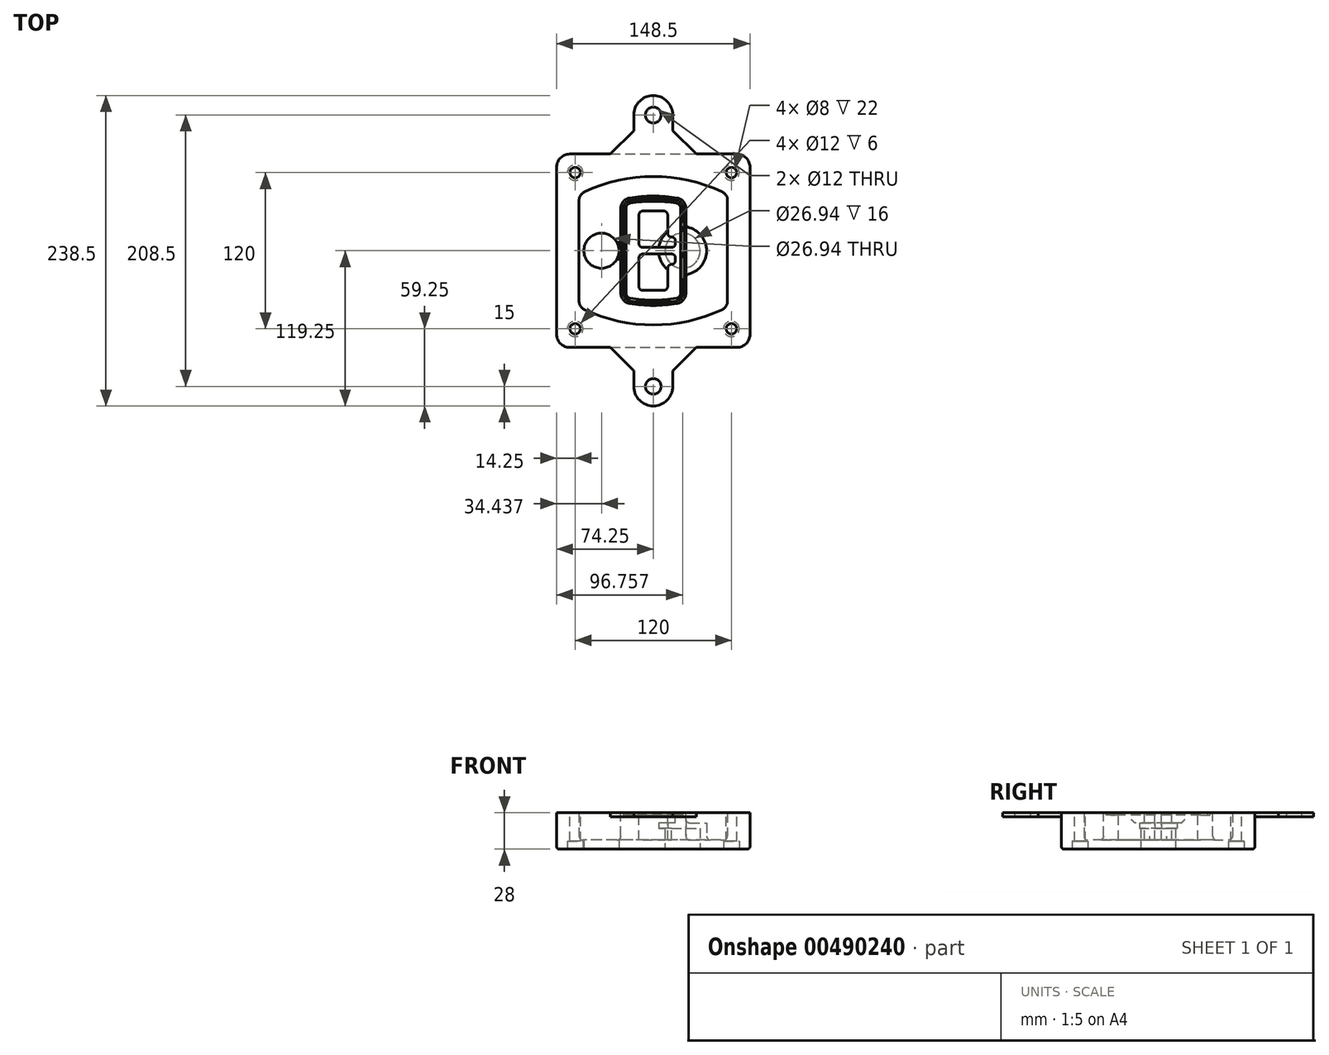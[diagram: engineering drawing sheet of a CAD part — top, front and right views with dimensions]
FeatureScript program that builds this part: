
annotation { "Feature Type Name" : "Feature", "Feature Type Description" : "" }
export const myFeature = defineFeature(function(context is Context, id is Id, definition is map)
    precondition{}
    {
        {
            var Q0;
            Q0=qCreatedBy(makeId("Top.planeOp"),FACE);
            var sketch = newSketch(context, id + "F0", { "sketchPlane" : qUnion([Q0])});
            skPoint(sketch, "E0.rect.middle", {"position": v(0, 0) * mm});
            skLineSegment(sketch, "E1.bottom", {"start": v(-64.25, -74.25) * mm, "end": v(64.25, -74.25) * mm});
            skLineSegment(sketch, "E1.top", {"start": v(-64.25, 74.25) * mm, "end": v(64.25, 74.25) * mm});
            skLineSegment(sketch, "E1.left", {"start": v(-74.25, -64.25) * mm, "end": v(-74.25, 64.25) * mm});
            skLineSegment(sketch, "E1.right", {"start": v(74.25, -64.25) * mm, "end": v(74.25, 64.25) * mm});
            skLineSegment(sketch, "E2", {"start": v(-74.25, 74.25) * mm, "end": v(74.25, -74.25) * mm, "construction": true});
            skLineSegment(sketch, "E3", {"start": v(74.25, 74.25) * mm, "end": v(-74.25, -74.25) * mm, "construction": true});
            skCircle(sketch, "E4", {"center": v(-60, 60) * mm, "radius": 4 * mm});
            skCircle(sketch, "E5", {"center": v(60, 60) * mm, "radius": 4 * mm});
            skCircle(sketch, "E6", {"center": v(60, -60) * mm, "radius": 4 * mm});
            skCircle(sketch, "E7", {"center": v(-60, -60) * mm, "radius": 4 * mm});
            skLineSegment(sketch, "E8", {"start": v(-60, 60) * mm, "end": v(60, 60) * mm, "construction": true});
            skLineSegment(sketch, "E9", {"start": v(60, 60) * mm, "end": v(60, -60) * mm, "construction": true});
            skLineSegment(sketch, "E10", {"start": v(60, -60) * mm, "end": v(-60, -60) * mm, "construction": true});
            skLineSegment(sketch, "E11", {"start": v(-60, -60) * mm, "end": v(-60, 60) * mm, "construction": true});
            skLineSegment(sketch, "E12", {"start": v(-60, 38.83) * mm, "end": v(-60, -38.83) * mm});
            skLineSegment(sketch, "E13", {"start": v(60, 38.83) * mm, "end": v(60, -38.83) * mm});
            skArc(sketch, "E14", {"start": v(54.26, 47.88) * mm, "mid": v(0, 60) * mm, "end": v(-54.26, 47.88) * mm});
            skArc(sketch, "E15", {"start": v(-54.26, -47.88) * mm, "mid": v(0, -60) * mm, "end": v(54.26, -47.88) * mm});
            skLineSegment(sketch, "E16", {"start": v(-60, 0) * mm, "end": v(60, 0) * mm, "construction": true});
            skPoint(sketch, "E17.visualSharp", {"position": v(-60, -45) * mm});
            skArc(sketch, "E17.filletArc", {"start": v(-60, -38.83) * mm, "mid": v(-58.44, -44.2) * mm, "end": v(-54.26, -47.88) * mm});
            skPoint(sketch, "E18.visualSharp", {"position": v(-60, 45) * mm});
            skArc(sketch, "E18.filletArc", {"start": v(-54.26, 47.88) * mm, "mid": v(-58.44, 44.2) * mm, "end": v(-60, 38.83) * mm});
            skPoint(sketch, "E19.visualSharp", {"position": v(60, 45) * mm});
            skArc(sketch, "E19.filletArc", {"start": v(60, 38.83) * mm, "mid": v(58.44, 44.2) * mm, "end": v(54.26, 47.88) * mm});
            skPoint(sketch, "E20.visualSharp", {"position": v(60, -45) * mm});
            skArc(sketch, "E20.filletArc", {"start": v(54.26, -47.88) * mm, "mid": v(58.44, -44.2) * mm, "end": v(60, -38.83) * mm});
            skPoint(sketch, "E21.visualSharp", {"position": v(-74.25, 74.25) * mm});
            skArc(sketch, "E21.filletArc", {"start": v(-64.25, 74.25) * mm, "mid": v(-71.32, 71.32) * mm, "end": v(-74.25, 64.25) * mm});
            skPoint(sketch, "E22.visualSharp", {"position": v(74.25, 74.25) * mm});
            skArc(sketch, "E22.filletArc", {"start": v(74.25, 64.25) * mm, "mid": v(71.32, 71.32) * mm, "end": v(64.25, 74.25) * mm});
            skPoint(sketch, "E23.visualSharp", {"position": v(74.25, -74.25) * mm});
            skArc(sketch, "E23.filletArc", {"start": v(64.25, -74.25) * mm, "mid": v(71.32, -71.32) * mm, "end": v(74.25, -64.25) * mm});
            skPoint(sketch, "E24.visualSharp", {"position": v(-74.25, -74.25) * mm});
            skArc(sketch, "E24.filletArc", {"start": v(-74.25, -64.25) * mm, "mid": v(-71.32, -71.32) * mm, "end": v(-64.25, -74.25) * mm});
            skArc(sketch, "E25.0", {"start": v(57, 38.83) * mm, "mid": v(55.9, 42.58) * mm, "end": v(52.98, 45.17) * mm});
            skLineSegment(sketch, "E25.1", {"start": v(57, 38.83) * mm, "end": v(57, -38.83) * mm});
            skArc(sketch, "E25.2", {"start": v(52.98, -45.17) * mm, "mid": v(55.9, -42.58) * mm, "end": v(57, -38.83) * mm});
            skArc(sketch, "E25.3", {"start": v(-52.98, -45.17) * mm, "mid": v(0, -57) * mm, "end": v(52.98, -45.17) * mm});
            skArc(sketch, "E25.4", {"start": v(-57, -38.83) * mm, "mid": v(-55.9, -42.58) * mm, "end": v(-52.98, -45.17) * mm});
            skArc(sketch, "E25.5", {"start": v(52.98, 45.17) * mm, "mid": v(0, 57) * mm, "end": v(-52.98, 45.17) * mm});
            skLineSegment(sketch, "E25.6", {"start": v(-57, 38.83) * mm, "end": v(-57, -38.83) * mm});
            skArc(sketch, "E25.7", {"start": v(-52.98, 45.17) * mm, "mid": v(-55.9, 42.58) * mm, "end": v(-57, 38.83) * mm});
            skArc(sketch, "E26.0", {"start": v(-55.96, 51.5) * mm, "mid": v(-61.82, 46.33) * mm, "end": v(-64, 38.83) * mm});
            skArc(sketch, "E26.1", {"start": v(55.96, 51.5) * mm, "mid": v(0, 64) * mm, "end": v(-55.96, 51.5) * mm});
            skArc(sketch, "E26.2", {"start": v(64, 38.83) * mm, "mid": v(61.82, 46.33) * mm, "end": v(55.96, 51.5) * mm});
            skLineSegment(sketch, "E26.3", {"start": v(64, 38.83) * mm, "end": v(64, -38.83) * mm});
            skArc(sketch, "E26.4", {"start": v(55.96, -51.5) * mm, "mid": v(61.82, -46.33) * mm, "end": v(64, -38.83) * mm});
            skLineSegment(sketch, "E26.5", {"start": v(-64, 38.83) * mm, "end": v(-64, -38.83) * mm});
            skArc(sketch, "E26.6", {"start": v(-55.96, -51.5) * mm, "mid": v(0, -64) * mm, "end": v(55.96, -51.5) * mm});
            skArc(sketch, "E26.7", {"start": v(-64, -38.83) * mm, "mid": v(-61.82, -46.33) * mm, "end": v(-55.96, -51.5) * mm});
            skSolve(sketch);
        }
        {
            var Q0;
            Q0=makeQuery(id+"F0.imprint","IMPRINT",FACE,{"disambiguationData":[TD([[makeQuery(id+"F0.imprint","IMPRINT",EDGE,{"derivedFrom":sQuery(id+"F0.wireOp",EDGE,"E1.bottom")}),1.0]])]});
            var Q1;
            Q1=makeQuery(id+"F0.imprint","IMPRINT",FACE,{"disambiguationData":[TD([[makeQuery(id+"F0.imprint","IMPRINT",EDGE,{"derivedFrom":sQuery(id+"F0.wireOp",EDGE,"E12")}),1.0]])]});
            var Q2;
            Q2=makeQuery(id+"F0.imprint","IMPRINT",FACE,{"disambiguationData":[TD([[makeQuery(id+"F0.imprint","IMPRINT",EDGE,{"derivedFrom":sQuery(id+"F0.wireOp",EDGE,"E25.0")}),1.0]])]});
            var Q3;
            Q3=makeQuery(id+"F0.imprint","IMPRINT",FACE,{"disambiguationData":[TD([[makeQuery(id+"F0.imprint","IMPRINT",EDGE,{"derivedFrom":sQuery(id+"F0.wireOp",EDGE,"E12")}),-1.0]])]});
            extrude(context, id + "F1", {"entities" : qUnion([Q0, Q1, Q2, Q3]), "oppositeDirection" : true, "depth" : 25 * mm});
        }
        {
            var Q0;
            Q0=makeQuery(id+"F0.imprint","IMPRINT",FACE,{"disambiguationData":[TD([[makeQuery(id+"F0.imprint","IMPRINT",EDGE,{"derivedFrom":sQuery(id+"F0.wireOp",EDGE,"E12")}),1.0]])]});
            extrude(context, id + "F2", {"entities" : qUnion([Q0]), "operationType" : NewBodyOperationType.ADD, "depth" : 3 * mm});
        }
        {
            var Q0;
            Q0=makeQuery(id+"F0.imprint","IMPRINT",FACE,{"disambiguationData":[TD([[makeQuery(id+"F0.imprint","IMPRINT",EDGE,{"derivedFrom":sQuery(id+"F0.wireOp",EDGE,"E25.0")}),1.0]])]});
            extrude(context, id + "F3", {"entities" : qUnion([Q0]), "operationType" : NewBodyOperationType.REMOVE, "oppositeDirection" : true, "depth" : 18 * mm});
        }
        {
            var Q0;
            Q0=makeQuery(id+"F2.opExtrude","CAP_FACE",FACE,{"disambiguationData":[OSD([sQuery(id+"F0.wireOp",EDGE,"E12"),sQuery(id+"F0.wireOp",EDGE,"E13"),sQuery(id+"F0.wireOp",EDGE,"E14"),sQuery(id+"F0.wireOp",EDGE,"E15"),sQuery(id+"F0.wireOp",EDGE,"E17.filletArc"),sQuery(id+"F0.wireOp",EDGE,"E18.filletArc"),sQuery(id+"F0.wireOp",EDGE,"E19.filletArc"),sQuery(id+"F0.wireOp",EDGE,"E20.filletArc"),sQuery(id+"F0.wireOp",EDGE,"E25.0"),sQuery(id+"F0.wireOp",EDGE,"E25.1"),sQuery(id+"F0.wireOp",EDGE,"E25.2"),sQuery(id+"F0.wireOp",EDGE,"E25.3"),sQuery(id+"F0.wireOp",EDGE,"E25.4"),sQuery(id+"F0.wireOp",EDGE,"E25.5"),sQuery(id+"F0.wireOp",EDGE,"E25.6"),sQuery(id+"F0.wireOp",EDGE,"E25.7")])],"isStart":false});
            var sketch = newSketch(context, id + "F4", { "sketchPlane" : qUnion([Q0])});
            skArc(sketch, "E27.0", {"start": v(-18.34, -40.45) * mm, "mid": v(0, -42) * mm, "end": v(18.34, -40.45) * mm});
            skArc(sketch, "E28.0", {"start": v(18.34, 40.45) * mm, "mid": v(0, 42) * mm, "end": v(-18.34, 40.45) * mm});
            skLineSegment(sketch, "E29", {"start": v(-25, 32.57) * mm, "end": v(-25, -32.57) * mm});
            skLineSegment(sketch, "E30", {"start": v(25, 32.57) * mm, "end": v(25, -32.57) * mm});
            skLineSegment(sketch, "E31", {"start": v(-25, 39.1) * mm, "end": v(25, 39.1) * mm, "construction": true});
            skLineSegment(sketch, "E32", {"start": v(-25, -39.1) * mm, "end": v(25, -39.1) * mm, "construction": true});
            skPoint(sketch, "E33.visualSharp", {"position": v(-25, 39.1) * mm});
            skArc(sketch, "E33.filletArc", {"start": v(-18.34, 40.45) * mm, "mid": v(-23.11, 37.73) * mm, "end": v(-25, 32.57) * mm});
            skPoint(sketch, "E34.visualSharp", {"position": v(25, 39.1) * mm});
            skArc(sketch, "E34.filletArc", {"start": v(25, 32.57) * mm, "mid": v(23.11, 37.73) * mm, "end": v(18.34, 40.45) * mm});
            skPoint(sketch, "E35.visualSharp", {"position": v(25, -39.1) * mm});
            skArc(sketch, "E35.filletArc", {"start": v(18.34, -40.45) * mm, "mid": v(23.11, -37.73) * mm, "end": v(25, -32.57) * mm});
            skPoint(sketch, "E36.visualSharp", {"position": v(-25, -39.1) * mm});
            skArc(sketch, "E36.filletArc", {"start": v(-25, -32.57) * mm, "mid": v(-23.11, -37.73) * mm, "end": v(-18.34, -40.45) * mm});
            skArc(sketch, "E37.0", {"start": v(52.98, 45.17) * mm, "mid": v(0, 57) * mm, "end": v(-52.98, 45.17) * mm});
            skArc(sketch, "E37.1", {"start": v(-52.98, 45.17) * mm, "mid": v(-55.9, 42.58) * mm, "end": v(-57, 38.83) * mm});
            skLineSegment(sketch, "E37.2", {"start": v(-57, 38.83) * mm, "end": v(-57, -38.83) * mm});
            skArc(sketch, "E37.3", {"start": v(-57, -38.83) * mm, "mid": v(-55.9, -42.58) * mm, "end": v(-52.98, -45.17) * mm});
            skArc(sketch, "E37.4", {"start": v(-52.98, -45.17) * mm, "mid": v(0, -57) * mm, "end": v(52.98, -45.17) * mm});
            skArc(sketch, "E37.5", {"start": v(52.98, -45.17) * mm, "mid": v(55.9, -42.58) * mm, "end": v(57, -38.83) * mm});
            skLineSegment(sketch, "E37.6", {"start": v(57, 38.83) * mm, "end": v(57, -38.83) * mm});
            skArc(sketch, "E37.7", {"start": v(57, 38.83) * mm, "mid": v(55.9, 42.58) * mm, "end": v(52.98, 45.17) * mm});
            skLineSegment(sketch, "E38.0", {"start": v(23, 32.57) * mm, "end": v(23, -32.57) * mm});
            skArc(sketch, "E38.1", {"start": v(18, -38.48) * mm, "mid": v(21.58, -36.44) * mm, "end": v(23, -32.57) * mm});
            skArc(sketch, "E38.2", {"start": v(-18, -38.48) * mm, "mid": v(0, -40) * mm, "end": v(18, -38.48) * mm});
            skArc(sketch, "E38.3", {"start": v(-23, -32.57) * mm, "mid": v(-21.58, -36.44) * mm, "end": v(-18, -38.48) * mm});
            skLineSegment(sketch, "E38.4", {"start": v(-23, 32.57) * mm, "end": v(-23, -32.57) * mm});
            skArc(sketch, "E38.5", {"start": v(23, 32.57) * mm, "mid": v(21.58, 36.44) * mm, "end": v(18, 38.48) * mm});
            skArc(sketch, "E38.6", {"start": v(-18, 38.48) * mm, "mid": v(-21.58, 36.44) * mm, "end": v(-23, 32.57) * mm});
            skArc(sketch, "E38.7", {"start": v(18, 38.48) * mm, "mid": v(0, 40) * mm, "end": v(-18, 38.48) * mm});
            skArc(sketch, "E39.0", {"start": v(21, 32.57) * mm, "mid": v(20.06, 35.15) * mm, "end": v(17.67, 36.5) * mm});
            skLineSegment(sketch, "E39.1", {"start": v(21, 32.57) * mm, "end": v(21, -32.57) * mm});
            skArc(sketch, "E39.2", {"start": v(17.67, -36.5) * mm, "mid": v(20.06, -35.15) * mm, "end": v(21, -32.57) * mm});
            skArc(sketch, "E39.3", {"start": v(-17.67, -36.5) * mm, "mid": v(0, -38) * mm, "end": v(17.67, -36.5) * mm});
            skArc(sketch, "E39.4", {"start": v(-21, -32.57) * mm, "mid": v(-20.06, -35.15) * mm, "end": v(-17.67, -36.5) * mm});
            skArc(sketch, "E39.5", {"start": v(17.67, 36.5) * mm, "mid": v(0, 38) * mm, "end": v(-17.67, 36.5) * mm});
            skLineSegment(sketch, "E39.6", {"start": v(-21, 32.57) * mm, "end": v(-21, -32.57) * mm});
            skArc(sketch, "E39.7", {"start": v(-17.67, 36.5) * mm, "mid": v(-20.06, 35.15) * mm, "end": v(-21, 32.57) * mm});
            skLineSegment(sketch, "E40", {"start": v(-25, 0) * mm, "end": v(25, 0) * mm, "construction": true});
            skLineSegment(sketch, "E41", {"start": v(-11, 5.5) * mm, "end": v(-11, 27.5) * mm});
            skLineSegment(sketch, "E42", {"start": v(-8, 30.5) * mm, "end": v(8, 30.5) * mm});
            skLineSegment(sketch, "E43", {"start": v(11, 27.5) * mm, "end": v(11, 13.5) * mm});
            skLineSegment(sketch, "E44", {"start": v(14, 10.5) * mm, "end": v(14, 10.5) * mm});
            skLineSegment(sketch, "E45", {"start": v(17, 7.5) * mm, "end": v(17, 5.5) * mm});
            skLineSegment(sketch, "E46", {"start": v(14, 2.5) * mm, "end": v(-8, 2.5) * mm});
            skPoint(sketch, "E47.visualSharp", {"position": v(-11, 30.5) * mm});
            skArc(sketch, "E47.filletArc", {"start": v(-8, 30.5) * mm, "mid": v(-10.12, 29.62) * mm, "end": v(-11, 27.5) * mm});
            skPoint(sketch, "E48.visualSharp", {"position": v(11, 30.5) * mm});
            skArc(sketch, "E48.filletArc", {"start": v(11, 27.5) * mm, "mid": v(10.12, 29.62) * mm, "end": v(8, 30.5) * mm});
            skPoint(sketch, "E49.visualSharp", {"position": v(11, 10.5) * mm});
            skArc(sketch, "E49.filletArc", {"start": v(11, 13.5) * mm, "mid": v(11.88, 11.38) * mm, "end": v(14, 10.5) * mm});
            skPoint(sketch, "E50.visualSharp", {"position": v(17, 10.5) * mm});
            skArc(sketch, "E50.filletArc", {"start": v(17, 7.5) * mm, "mid": v(16.12, 9.62) * mm, "end": v(14, 10.5) * mm});
            skPoint(sketch, "E51.visualSharp", {"position": v(17, 2.5) * mm});
            skArc(sketch, "E51.filletArc", {"start": v(14, 2.5) * mm, "mid": v(16.12, 3.38) * mm, "end": v(17, 5.5) * mm});
            skPoint(sketch, "E52.visualSharp", {"position": v(-11, 2.5) * mm});
            skArc(sketch, "E52.filletArc", {"start": v(-11, 5.5) * mm, "mid": v(-10.12, 3.38) * mm, "end": v(-8, 2.5) * mm});
            skLineSegment(sketch, "E53.0.MirrorCS", {"start": v(14, -2.5) * mm, "end": v(-8, -2.5) * mm});
            skArc(sketch, "E54.0.MirrorCS", {"start": v(-11, -5.5) * mm, "mid": v(-10.12, -3.38) * mm, "end": v(-8, -2.5) * mm});
            skLineSegment(sketch, "E55.0.MirrorCS", {"start": v(-11, -5.5) * mm, "end": v(-11, -27.5) * mm});
            skArc(sketch, "E56.0.MirrorCS", {"start": v(-8, -30.5) * mm, "mid": v(-10.12, -29.62) * mm, "end": v(-11, -27.5) * mm});
            skLineSegment(sketch, "E57.0.MirrorCS", {"start": v(-8, -30.5) * mm, "end": v(8, -30.5) * mm});
            skArc(sketch, "E58.0.MirrorCS", {"start": v(11, -27.5) * mm, "mid": v(10.12, -29.62) * mm, "end": v(8, -30.5) * mm});
            skLineSegment(sketch, "E59.0.MirrorCS", {"start": v(11, -27.5) * mm, "end": v(11, -13.5) * mm});
            skArc(sketch, "E60.0.MirrorCS", {"start": v(11, -13.5) * mm, "mid": v(11.88, -11.38) * mm, "end": v(14, -10.5) * mm});
            skArc(sketch, "E61.0.MirrorCS", {"start": v(17, -7.5) * mm, "mid": v(16.12, -9.62) * mm, "end": v(14, -10.5) * mm});
            skLineSegment(sketch, "E62.0.MirrorCS", {"start": v(17, -7.5) * mm, "end": v(17, -5.5) * mm});
            skArc(sketch, "E63.0.MirrorCS", {"start": v(14, -2.5) * mm, "mid": v(16.12, -3.38) * mm, "end": v(17, -5.5) * mm});
            skSolve(sketch);
        }
        {
            var Q0;
            Q0=makeQuery(id+"F4.imprint","IMPRINT",FACE,{"disambiguationData":[TD([[makeQuery(id+"F4.imprint","IMPRINT",EDGE,{"derivedFrom":sQuery(id+"F4.wireOp",EDGE,"E27.0")}),1.0]])]});
            var Q1;
            Q1=makeQuery(id+"F4.imprint","IMPRINT",FACE,{"disambiguationData":[TD([[makeQuery(id+"F4.imprint","IMPRINT",EDGE,{"derivedFrom":sQuery(id+"F4.wireOp",EDGE,"E38.0")}),-1.0]])]});
            var Q2;
            Q2=makeQuery(id+"F4.imprint","IMPRINT",FACE,{"disambiguationData":[TD([[makeQuery(id+"F4.imprint","IMPRINT",EDGE,{"derivedFrom":sQuery(id+"F4.wireOp",EDGE,"E39.0")}),1.0]])]});
            extrude(context, id + "F5", {"entities" : qUnion([Q0, Q1, Q2]), "operationType" : NewBodyOperationType.ADD, "endBound" : BoundingType.UP_TO_NEXT, "oppositeDirection" : true, "depth" : 25 * mm});
        }
        {
            var Q0;
            Q0=makeQuery(id+"F4.imprint","IMPRINT",FACE,{"disambiguationData":[TD([[makeQuery(id+"F4.imprint","IMPRINT",EDGE,{"derivedFrom":sQuery(id+"F4.wireOp",EDGE,"E38.0")}),-1.0]])]});
            extrude(context, id + "F6", {"entities" : qUnion([Q0]), "operationType" : NewBodyOperationType.REMOVE, "oppositeDirection" : true, "depth" : 2 * mm});
        }
        {
            var Q0;
            Q0=makeQuery(id+"F1.opExtrude","CAP_FACE",FACE,{"disambiguationData":[OSD([sQuery(id+"F0.wireOp",EDGE,"E1.bottom"),sQuery(id+"F0.wireOp",EDGE,"E1.top"),sQuery(id+"F0.wireOp",EDGE,"E1.left"),sQuery(id+"F0.wireOp",EDGE,"E1.right"),sQuery(id+"F0.wireOp",EDGE,"E4"),sQuery(id+"F0.wireOp",EDGE,"E5"),sQuery(id+"F0.wireOp",EDGE,"E6"),sQuery(id+"F0.wireOp",EDGE,"E7"),sQuery(id+"F0.wireOp",EDGE,"E21.filletArc"),sQuery(id+"F0.wireOp",EDGE,"E22.filletArc"),sQuery(id+"F0.wireOp",EDGE,"E23.filletArc"),sQuery(id+"F0.wireOp",EDGE,"E24.filletArc")])],"isStart":false});
            var sketch = newSketch(context, id + "F7", { "sketchPlane" : qUnion([Q0])});
            skCircle(sketch, "E64", {"center": v(22.5, 0) * mm, "radius": 13.47 * mm});
            skCircle(sketch, "E65", {"center": v(-39.81, 0) * mm, "radius": 13.47 * mm});
            skLineSegment(sketch, "E66", {"start": v(74.25, 0) * mm, "end": v(-74.25, 0) * mm});
            skCircle(sketch, "E67", {"center": v(22.5, 0) * mm, "radius": 18.47 * mm});
            skCircle(sketch, "E68", {"center": v(60, -60) * mm, "radius": 6 * mm});
            skCircle(sketch, "E69", {"center": v(-60, -60) * mm, "radius": 6 * mm});
            skCircle(sketch, "E70", {"center": v(-60, 60) * mm, "radius": 6 * mm});
            skCircle(sketch, "E71", {"center": v(60, 60) * mm, "radius": 6 * mm});
            skSolve(sketch);
        }
        {
            var Q0;
            {var subQ1=sQuery(id+"F7.wireOp",EDGE,"E66");var subQ4=sQuery(id+"F7.wireOp",EDGE,"E64");var subQ6=makeQuery(id+"F7.imprint","INTERSECT",VERTEX,{"disambiguationData":[OD(0.0)],"derivedFrom":[subQ4,subQ1]});Q0=makeQuery(id+"F7.imprint","IMPRINT",FACE,{"disambiguationData":[TD([[makeQuery(id+"F7.imprint","IMPRINT",EDGE,{"disambiguationData":[TD([[subQ6,-1.0]])],"derivedFrom":subQ4}),-1.0]])]});}
            var Q1;
            {var subQ0=sQuery(id+"F7.wireOp",EDGE,"E66");var subQ1=sQuery(id+"F7.wireOp",EDGE,"E64");var subQ3=makeQuery(id+"F7.imprint","INTERSECT",VERTEX,{"disambiguationData":[OD(0.0)],"derivedFrom":[subQ1,subQ0]});Q1=makeQuery(id+"F7.imprint","IMPRINT",FACE,{"disambiguationData":[TD([[makeQuery(id+"F7.imprint","IMPRINT",EDGE,{"disambiguationData":[TD([[subQ3,-1.0]])],"derivedFrom":subQ1}),1.0]])]});}
            var Q2;
            {var subQ0=sQuery(id+"F7.wireOp",EDGE,"E66");var subQ1=sQuery(id+"F7.wireOp",EDGE,"E64");var subQ3=makeQuery(id+"F7.imprint","INTERSECT",VERTEX,{"disambiguationData":[OD(0.0)],"derivedFrom":[subQ1,subQ0]});Q2=makeQuery(id+"F7.imprint","IMPRINT",FACE,{"disambiguationData":[TD([[makeQuery(id+"F7.imprint","IMPRINT",EDGE,{"disambiguationData":[TD([[subQ3,1.0]])],"derivedFrom":subQ1}),1.0]])]});}
            var Q3;
            {var subQ1=sQuery(id+"F7.wireOp",EDGE,"E66");var subQ4=sQuery(id+"F7.wireOp",EDGE,"E64");var subQ6=makeQuery(id+"F7.imprint","INTERSECT",VERTEX,{"disambiguationData":[OD(0.0)],"derivedFrom":[subQ4,subQ1]});Q3=makeQuery(id+"F7.imprint","IMPRINT",FACE,{"disambiguationData":[TD([[makeQuery(id+"F7.imprint","IMPRINT",EDGE,{"disambiguationData":[TD([[subQ6,1.0]])],"derivedFrom":subQ4}),-1.0]])]});}
            extrude(context, id + "F8", {"entities" : qUnion([Q0, Q1, Q2, Q3]), "operationType" : NewBodyOperationType.ADD, "oppositeDirection" : true, "depth" : 20 * mm});
        }
        {
            var Q0;
            {var subQ0=sQuery(id+"F7.wireOp",EDGE,"E66");var subQ1=sQuery(id+"F7.wireOp",EDGE,"E64");var subQ3=makeQuery(id+"F7.imprint","INTERSECT",VERTEX,{"disambiguationData":[OD(0.0)],"derivedFrom":[subQ1,subQ0]});Q0=makeQuery(id+"F7.imprint","IMPRINT",FACE,{"disambiguationData":[TD([[makeQuery(id+"F7.imprint","IMPRINT",EDGE,{"disambiguationData":[TD([[subQ3,-1.0]])],"derivedFrom":subQ1}),1.0]])]});}
            var Q1;
            {var subQ0=sQuery(id+"F7.wireOp",EDGE,"E66");var subQ1=sQuery(id+"F7.wireOp",EDGE,"E64");var subQ3=makeQuery(id+"F7.imprint","INTERSECT",VERTEX,{"disambiguationData":[OD(0.0)],"derivedFrom":[subQ1,subQ0]});Q1=makeQuery(id+"F7.imprint","IMPRINT",FACE,{"disambiguationData":[TD([[makeQuery(id+"F7.imprint","IMPRINT",EDGE,{"disambiguationData":[TD([[subQ3,1.0]])],"derivedFrom":subQ1}),1.0]])]});}
            extrude(context, id + "F9", {"entities" : qUnion([Q0, Q1]), "operationType" : NewBodyOperationType.REMOVE, "oppositeDirection" : true, "depth" : 16 * mm});
        }
        {
            var Q0;
            {var subQ0=sQuery(id+"F7.wireOp",EDGE,"E66");var subQ1=sQuery(id+"F7.wireOp",EDGE,"E65");var subQ3=makeQuery(id+"F7.imprint","INTERSECT",VERTEX,{"disambiguationData":[OD(0.0)],"derivedFrom":[subQ1,subQ0]});Q0=makeQuery(id+"F7.imprint","IMPRINT",FACE,{"disambiguationData":[TD([[makeQuery(id+"F7.imprint","IMPRINT",EDGE,{"disambiguationData":[TD([[subQ3,-1.0]])],"derivedFrom":subQ1}),1.0]])]});}
            var Q1;
            {var subQ0=sQuery(id+"F7.wireOp",EDGE,"E66");var subQ1=sQuery(id+"F7.wireOp",EDGE,"E65");var subQ3=makeQuery(id+"F7.imprint","INTERSECT",VERTEX,{"disambiguationData":[OD(0.0)],"derivedFrom":[subQ1,subQ0]});Q1=makeQuery(id+"F7.imprint","IMPRINT",FACE,{"disambiguationData":[TD([[makeQuery(id+"F7.imprint","IMPRINT",EDGE,{"disambiguationData":[TD([[subQ3,1.0]])],"derivedFrom":subQ1}),1.0]])]});}
            extrude(context, id + "F10", {"entities" : qUnion([Q0, Q1]), "operationType" : NewBodyOperationType.REMOVE, "oppositeDirection" : true, "depth" : 25 * mm});
        }
        {
            var Q0;
            Q0=makeQuery(id+"F7.imprint","IMPRINT",FACE,{"disambiguationData":[TD([[makeQuery(id+"F7.imprint","IMPRINT",EDGE,{"derivedFrom":sQuery(id+"F7.wireOp",EDGE,"E68")}),1.0]])]});
            var Q1;
            Q1=makeQuery(id+"F7.imprint","IMPRINT",FACE,{"disambiguationData":[TD([[makeQuery(id+"F7.imprint","IMPRINT",EDGE,{"derivedFrom":makeQuery(id+"F1.opExtrude","CAP_EDGE",EDGE,{"disambiguationData":[OSD([sQuery(id+"F0.wireOp",EDGE,"E5")])],"isStart":false})}),-1.0]])]});
            var Q2;
            Q2=makeQuery(id+"F7.imprint","IMPRINT",FACE,{"disambiguationData":[TD([[makeQuery(id+"F7.imprint","IMPRINT",EDGE,{"derivedFrom":sQuery(id+"F7.wireOp",EDGE,"E69")}),1.0]])]});
            var Q3;
            Q3=makeQuery(id+"F7.imprint","IMPRINT",FACE,{"disambiguationData":[TD([[makeQuery(id+"F7.imprint","IMPRINT",EDGE,{"derivedFrom":makeQuery(id+"F1.opExtrude","CAP_EDGE",EDGE,{"disambiguationData":[OSD([sQuery(id+"F0.wireOp",EDGE,"E4")])],"isStart":false})}),-1.0]])]});
            var Q4;
            Q4=makeQuery(id+"F7.imprint","IMPRINT",FACE,{"disambiguationData":[TD([[makeQuery(id+"F7.imprint","IMPRINT",EDGE,{"derivedFrom":sQuery(id+"F7.wireOp",EDGE,"E70")}),1.0]])]});
            var Q5;
            Q5=makeQuery(id+"F7.imprint","IMPRINT",FACE,{"disambiguationData":[TD([[makeQuery(id+"F7.imprint","IMPRINT",EDGE,{"derivedFrom":makeQuery(id+"F1.opExtrude","CAP_EDGE",EDGE,{"disambiguationData":[OSD([sQuery(id+"F0.wireOp",EDGE,"E7")])],"isStart":false})}),-1.0]])]});
            var Q6;
            Q6=makeQuery(id+"F7.imprint","IMPRINT",FACE,{"disambiguationData":[TD([[makeQuery(id+"F7.imprint","IMPRINT",EDGE,{"derivedFrom":sQuery(id+"F7.wireOp",EDGE,"E71")}),1.0]])]});
            var Q7;
            Q7=makeQuery(id+"F7.imprint","IMPRINT",FACE,{"disambiguationData":[TD([[makeQuery(id+"F7.imprint","IMPRINT",EDGE,{"derivedFrom":makeQuery(id+"F1.opExtrude","CAP_EDGE",EDGE,{"disambiguationData":[OSD([sQuery(id+"F0.wireOp",EDGE,"E6")])],"isStart":false})}),-1.0]])]});
            extrude(context, id + "F11", {"entities" : qUnion([Q0, Q1, Q2, Q3, Q4, Q5, Q6, Q7]), "operationType" : NewBodyOperationType.REMOVE, "oppositeDirection" : true, "depth" : 6 * mm});
        }
        {
            var Q0;
            Q0=makeQuery(id+"F9.boolean.opBoolean","COPY",FACE,{"derivedFrom":makeQuery(id+"F9.opExtrude","CAP_FACE",FACE,{"disambiguationData":[OSD([sQuery(id+"F7.wireOp",EDGE,"E64")])],"isStart":false})});
            var sketch = newSketch(context, id + "F12", { "sketchPlane" : qUnion([Q0])});
            skArc(sketch, "E72.0", {"start": v(11, 14.45) * mm, "mid": v(6.45, 9.13) * mm, "end": v(4.2, 2.5) * mm});
            skArc(sketch, "E72.1", {"start": v(4.2, -2.5) * mm, "mid": v(6.45, -9.13) * mm, "end": v(11, -14.45) * mm});
            skLineSegment(sketch, "E73", {"start": v(4.2, -2.5) * mm, "end": v(14, -2.5) * mm});
            skLineSegment(sketch, "E74.0", {"start": v(14, 2.5) * mm, "end": v(4.2, 2.5) * mm});
            skArc(sketch, "E74.1", {"start": v(14, 2.5) * mm, "mid": v(16.12, 3.38) * mm, "end": v(17, 5.5) * mm});
            skLineSegment(sketch, "E74.2", {"start": v(17, 7.5) * mm, "end": v(17, 5.5) * mm});
            skArc(sketch, "E74.3", {"start": v(17, 7.5) * mm, "mid": v(16.12, 9.62) * mm, "end": v(14, 10.5) * mm});
            skArc(sketch, "E74.4", {"start": v(11, 13.5) * mm, "mid": v(11.88, 11.38) * mm, "end": v(14, 10.5) * mm});
            skLineSegment(sketch, "E74.5", {"start": v(11, 14.45) * mm, "end": v(11, 13.5) * mm});
            skLineSegment(sketch, "E74.7", {"start": v(14, -2.5) * mm, "end": v(4.2, -2.5) * mm});
            skArc(sketch, "E74.8", {"start": v(14, -2.5) * mm, "mid": v(16.12, -3.38) * mm, "end": v(17, -5.5) * mm});
            skLineSegment(sketch, "E74.9", {"start": v(17, -7.5) * mm, "end": v(17, -5.5) * mm});
            skArc(sketch, "E74.10", {"start": v(17, -7.5) * mm, "mid": v(16.12, -9.62) * mm, "end": v(14, -10.5) * mm});
            skArc(sketch, "E74.11", {"start": v(11, -13.5) * mm, "mid": v(11.88, -11.38) * mm, "end": v(14, -10.5) * mm});
            skLineSegment(sketch, "E74.12", {"start": v(11, -14.45) * mm, "end": v(11, -13.5) * mm});
            skPoint(sketch, "E75.orphan", {"position": v(11, -27.5) * mm});
            skPoint(sketch, "E76.orphan", {"position": v(-8, -2.5) * mm});
            skPoint(sketch, "E77.orphan", {"position": v(-8, 2.5) * mm});
            skPoint(sketch, "E78.orphan", {"position": v(11, 27.5) * mm});
            skSolve(sketch);
        }
        {
            var Q0;
            {var subQ7=sQuery(id+"F12.wireOp",EDGE,"E72.0");var subQ14=sQuery(id+"F12.wireOp",EDGE,"E72.1");var subQ16=sQuery(id+"F12.wireOp",EDGE,"E74.1");var subQ18=sQuery(id+"F12.wireOp",EDGE,"E74.8");Q0=qUnion([makeQuery(id+"F12.imprint","IMPRINT",FACE,{"disambiguationData":[TD([[makeQuery(id+"F12.imprint","IMPRINT",EDGE,{"derivedFrom":subQ7}),1.0]])]}),makeQuery(id+"F12.imprint","IMPRINT",FACE,{"disambiguationData":[TD([[makeQuery(id+"F12.imprint","IMPRINT",EDGE,{"derivedFrom":subQ14}),1.0]])]}),makeQuery(id+"F12.imprint","IMPRINT",FACE,{"disambiguationData":[TD([[makeQuery(id+"F12.imprint","IMPRINT",EDGE,{"derivedFrom":subQ16}),1.0]])]}),makeQuery(id+"F12.imprint","IMPRINT",FACE,{"disambiguationData":[TD([[makeQuery(id+"F12.imprint","IMPRINT",EDGE,{"derivedFrom":subQ18}),-1.0]])]})]);}
            var Q1;
            Q1=makeQuery(id+"F5.boolean.opBoolean","SPLIT",FACE,{"disambiguationData":[TD([makeQuery(id+"F5.opExtrude","SWEPT_FACE",FACE,{"disambiguationData":[OSD([sQuery(id+"F4.wireOp",EDGE,"E41")])]})])],"derivedFrom":makeQuery(id+"F3.boolean.opBoolean","COPY",FACE,{"derivedFrom":makeQuery(id+"F3.opExtrude","CAP_FACE",FACE,{"disambiguationData":[OSD([sQuery(id+"F0.wireOp",EDGE,"E25.0"),sQuery(id+"F0.wireOp",EDGE,"E25.1"),sQuery(id+"F0.wireOp",EDGE,"E25.2"),sQuery(id+"F0.wireOp",EDGE,"E25.3"),sQuery(id+"F0.wireOp",EDGE,"E25.4"),sQuery(id+"F0.wireOp",EDGE,"E25.5"),sQuery(id+"F0.wireOp",EDGE,"E25.6"),sQuery(id+"F0.wireOp",EDGE,"E25.7")])],"isStart":false})})});
            extrude(context, id + "F13", {"entities" : qUnion([Q0]), "operationType" : NewBodyOperationType.REMOVE, "endBound" : BoundingType.UP_TO_SURFACE, "endBoundEntityFace" : qUnion([Q1]), "depth" : 25 * mm});
        }
        {
            var Q0;
            Q0=makeQuery(id+"F3.boolean.opBoolean","COPY",EDGE,{"derivedFrom":makeQuery(id+"F3.opExtrude","CAP_EDGE",EDGE,{"disambiguationData":[OSD([sQuery(id+"F0.wireOp",EDGE,"E25.6")])],"isStart":false})});
            var Q1;
            Q1=makeQuery(id+"F8.boolean.opBoolean","INTERSECT",EDGE,{"derivedFrom":[makeQuery(id+"F5.opExtrude","SWEPT_FACE",FACE,{"disambiguationData":[OSD([sQuery(id+"F4.wireOp",EDGE,"E30")])]}),makeQuery(id+"F8.opExtrude","CAP_FACE",FACE,{"disambiguationData":[OSD([sQuery(id+"F7.wireOp",EDGE,"E67")])],"isStart":false})]});
            var Q2;
            Q2=makeQuery(id+"F8.boolean.opBoolean","INTERSECT",EDGE,{"disambiguationData":[OD(1.0)],"derivedFrom":[makeQuery(id+"F5.opExtrude","SWEPT_FACE",FACE,{"disambiguationData":[OSD([sQuery(id+"F4.wireOp",EDGE,"E30")])]}),makeQuery(id+"F8.opExtrude","SWEPT_FACE",FACE,{"disambiguationData":[OSD([sQuery(id+"F7.wireOp",EDGE,"E67")])]})]});
            var Q3;
            {var subQ0=sQuery(id+"F4.wireOp",EDGE,"E30");Q3=makeQuery(id+"F8.boolean.opBoolean","SPLIT",EDGE,{"disambiguationData":[TD([makeQuery(id+"F5.opExtrude","SWEPT_FACE",FACE,{"disambiguationData":[OSD([sQuery(id+"F4.wireOp",EDGE,"E35.filletArc")])]})])],"derivedFrom":makeQuery(id+"F5.opExtrude","CAP_EDGE",EDGE,{"disambiguationData":[OSD([subQ0])],"isStart":false})});}
            var Q4;
            {var subQ0=sQuery(id+"F0.wireOp",EDGE,"E25.7");var subQ1=sQuery(id+"F0.wireOp",EDGE,"E25.1");var subQ2=sQuery(id+"F0.wireOp",EDGE,"E25.6");var subQ3=sQuery(id+"F0.wireOp",EDGE,"E25.5");var subQ4=sQuery(id+"F0.wireOp",EDGE,"E25.4");var subQ5=sQuery(id+"F0.wireOp",EDGE,"E25.0");var subQ6=sQuery(id+"F0.wireOp",EDGE,"E25.2");var subQ7=sQuery(id+"F0.wireOp",EDGE,"E25.3");Q4=makeQuery(id+"F8.boolean.opBoolean","INTERSECT",EDGE,{"derivedFrom":[makeQuery(id+"F5.boolean.opBoolean","SPLIT",FACE,{"disambiguationData":[TD([makeQuery(id+"F2.opExtrude","SWEPT_FACE",FACE,{"disambiguationData":[OSD([subQ5])]})])],"derivedFrom":makeQuery(id+"F3.boolean.opBoolean","COPY",FACE,{"derivedFrom":makeQuery(id+"F3.opExtrude","CAP_FACE",FACE,{"disambiguationData":[OSD([subQ5,subQ1,subQ6,subQ7,subQ4,subQ3,subQ2,subQ0])],"isStart":false})})}),makeQuery(id+"F8.opExtrude","SWEPT_FACE",FACE,{"disambiguationData":[OSD([sQuery(id+"F7.wireOp",EDGE,"E67")])]})]});}
            var Q5;
            Q5=makeQuery(id+"F8.boolean.opBoolean","INTERSECT",EDGE,{"disambiguationData":[OD(0.0)],"derivedFrom":[makeQuery(id+"F5.opExtrude","SWEPT_FACE",FACE,{"disambiguationData":[OSD([sQuery(id+"F4.wireOp",EDGE,"E30")])]}),makeQuery(id+"F8.opExtrude","SWEPT_FACE",FACE,{"disambiguationData":[OSD([sQuery(id+"F7.wireOp",EDGE,"E67")])]})]});
            fillet(context, id + "F14", {"entities" : qUnion([Q0, Q1, Q2, Q3, Q4, Q5]), "radius" : 3 * mm, "tangentPropagation" : true, "allowEdgeOverflow" : false});
        }
        {
            var Q0;
            Q0=makeQuery(id+"F1.opExtrude","CAP_EDGE",EDGE,{"disambiguationData":[OSD([sQuery(id+"F0.wireOp",EDGE,"E1.bottom")])],"isStart":false});
            fillet(context, id + "F15", {"entities" : qUnion([Q0]), "radius" : 2 * mm, "tangentPropagation" : true, "allowEdgeOverflow" : false});
        }
        {
            var Q0;
            {var subQ0=sQuery(id+"F0.wireOp",EDGE,"E21.filletArc");var subQ1=sQuery(id+"F0.wireOp",EDGE,"E7");var subQ2=sQuery(id+"F0.wireOp",EDGE,"E6");var subQ3=sQuery(id+"F0.wireOp",EDGE,"E5");var subQ4=sQuery(id+"F0.wireOp",EDGE,"E4");var subQ5=sQuery(id+"F0.wireOp",EDGE,"E22.filletArc");var subQ6=sQuery(id+"F0.wireOp",EDGE,"E1.bottom");var subQ7=sQuery(id+"F0.wireOp",EDGE,"E1.right");var subQ8=sQuery(id+"F0.wireOp",EDGE,"E1.top");var subQ9=sQuery(id+"F0.wireOp",EDGE,"E1.left");var subQ10=sQuery(id+"F0.wireOp",EDGE,"E23.filletArc");var subQ11=sQuery(id+"F0.wireOp",EDGE,"E24.filletArc");Q0=makeQuery(id+"F2.boolean.opBoolean","SPLIT",FACE,{"disambiguationData":[TD([makeQuery(id+"F1.opExtrude","SWEPT_FACE",FACE,{"disambiguationData":[OSD([subQ6])]})])],"derivedFrom":makeQuery(id+"F1.opExtrude","CAP_FACE",FACE,{"disambiguationData":[OSD([subQ6,subQ8,subQ9,subQ7,subQ4,subQ3,subQ2,subQ1,subQ0,subQ5,subQ10,subQ11])],"isStart":true})});}
            var sketch = newSketch(context, id + "F16", { "sketchPlane" : qUnion([Q0])});
            skLineSegment(sketch, "E79", {"start": v(0, 74.25) * mm, "end": v(0, 104.25) * mm, "construction": true});
            skArc(sketch, "E80", {"start": v(15, 104.25) * mm, "mid": v(0, 119.25) * mm, "end": v(-15, 104.25) * mm});
            skLineSegment(sketch, "E81", {"start": v(15, 104.25) * mm, "end": v(15, 92.25) * mm});
            skLineSegment(sketch, "E82", {"start": v(-15, 104.25) * mm, "end": v(-15, 92.25) * mm});
            skLineSegment(sketch, "E83", {"start": v(-15, 92.25) * mm, "end": v(-33, 74.25) * mm});
            skLineSegment(sketch, "E84", {"start": v(15, 92.25) * mm, "end": v(33, 74.25) * mm});
            skCircle(sketch, "E85", {"center": v(0, 104.25) * mm, "radius": 6 * mm});
            skLineSegment(sketch, "E86", {"start": v(-83.4, 0) * mm, "end": v(85.63, 0) * mm, "construction": true});
            skPoint(sketch, "E86.endSnap0", {"position": v(74.25, 0) * mm});
            skLineSegment(sketch, "E87.MirrorCS", {"start": v(15, -104.25) * mm, "end": v(15, -92.25) * mm});
            skLineSegment(sketch, "E88.MirrorCS", {"start": v(-15, -104.25) * mm, "end": v(-15, -92.25) * mm});
            skCircle(sketch, "E89.MirrorC", {"center": v(0, -104.25) * mm, "radius": 6 * mm});
            skArc(sketch, "E90.MirrorCS", {"start": v(15, -104.25) * mm, "mid": v(0, -119.25) * mm, "end": v(-15, -104.25) * mm});
            skLineSegment(sketch, "E91.MirrorCS", {"start": v(-15, -92.25) * mm, "end": v(-33, -74.25) * mm});
            skLineSegment(sketch, "E92.MirrorCS", {"start": v(0, -74.25) * mm, "end": v(0, -104.25) * mm, "construction": true});
            skLineSegment(sketch, "E93.MirrorCS", {"start": v(15, -92.25) * mm, "end": v(33, -74.25) * mm});
            skSolve(sketch);
        }
        {
            var Q0;
            Q0=makeQuery(id+"F16.imprint","IMPRINT",FACE,{"disambiguationData":[TD([[makeQuery(id+"F16.imprint","IMPRINT",EDGE,{"derivedFrom":sQuery(id+"F16.wireOp",EDGE,"E80")}),1.0]])]});
            var Q1;
            Q1=makeQuery(id+"F16.imprint","IMPRINT",FACE,{"disambiguationData":[TD([[makeQuery(id+"F16.imprint","IMPRINT",EDGE,{"derivedFrom":makeQuery(id+"F1.opExtrude","CAP_EDGE",EDGE,{"disambiguationData":[OSD([sQuery(id+"F0.wireOp",EDGE,"E1.left")])],"isStart":true})}),-1.0]])]});
            var Q2;
            Q2=makeQuery(id+"F16.imprint","IMPRINT",FACE,{"disambiguationData":[TD([[makeQuery(id+"F16.imprint","IMPRINT",EDGE,{"derivedFrom":sQuery(id+"F16.wireOp",EDGE,"E87.MirrorCS")}),1.0]])]});
            var Q3;
            {var subQ0=sQuery(id+"F4.wireOp",EDGE,"E36.filletArc");var subQ1=sQuery(id+"F4.wireOp",EDGE,"E35.filletArc");var subQ2=sQuery(id+"F4.wireOp",EDGE,"E34.filletArc");var subQ3=sQuery(id+"F4.wireOp",EDGE,"E33.filletArc");var subQ4=sQuery(id+"F4.wireOp",EDGE,"E27.0");var subQ5=sQuery(id+"F4.wireOp",EDGE,"E30");var subQ6=sQuery(id+"F4.wireOp",EDGE,"E28.0");var subQ7=sQuery(id+"F4.wireOp",EDGE,"E29");Q3=makeQuery(id+"F6.boolean.opBoolean","SPLIT",FACE,{"disambiguationData":[TD([makeQuery(id+"F5.opExtrude","SWEPT_FACE",FACE,{"disambiguationData":[OSD([subQ4])]})])],"derivedFrom":makeQuery(id+"F5.opExtrude","CAP_FACE",FACE,{"disambiguationData":[OSD([subQ4,subQ6,subQ7,subQ5,subQ3,subQ2,subQ1,subQ0,sQuery(id+"F4.wireOp",EDGE,"E41"),sQuery(id+"F4.wireOp",EDGE,"E42"),sQuery(id+"F4.wireOp",EDGE,"E43"),sQuery(id+"F4.wireOp",EDGE,"E45"),sQuery(id+"F4.wireOp",EDGE,"E46"),sQuery(id+"F4.wireOp",EDGE,"E47.filletArc"),sQuery(id+"F4.wireOp",EDGE,"E48.filletArc"),sQuery(id+"F4.wireOp",EDGE,"E49.filletArc"),sQuery(id+"F4.wireOp",EDGE,"E50.filletArc"),sQuery(id+"F4.wireOp",EDGE,"E51.filletArc"),sQuery(id+"F4.wireOp",EDGE,"E52.filletArc"),sQuery(id+"F4.wireOp",EDGE,"E53.0.MirrorCS"),sQuery(id+"F4.wireOp",EDGE,"E54.0.MirrorCS"),sQuery(id+"F4.wireOp",EDGE,"E55.0.MirrorCS"),sQuery(id+"F4.wireOp",EDGE,"E56.0.MirrorCS"),sQuery(id+"F4.wireOp",EDGE,"E57.0.MirrorCS"),sQuery(id+"F4.wireOp",EDGE,"E58.0.MirrorCS"),sQuery(id+"F4.wireOp",EDGE,"E59.0.MirrorCS"),sQuery(id+"F4.wireOp",EDGE,"E60.0.MirrorCS"),sQuery(id+"F4.wireOp",EDGE,"E61.0.MirrorCS"),sQuery(id+"F4.wireOp",EDGE,"E62.0.MirrorCS"),sQuery(id+"F4.wireOp",EDGE,"E63.0.MirrorCS")])],"isStart":true})});}
            extrude(context, id + "F17", {"entities" : qUnion([Q0, Q1, Q2]), "operationType" : NewBodyOperationType.ADD, "endBound" : BoundingType.UP_TO_SURFACE, "endBoundEntityFace" : qUnion([Q3]), "depth" : 25 * mm});
        }
    });
